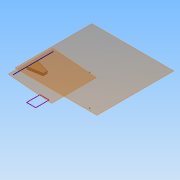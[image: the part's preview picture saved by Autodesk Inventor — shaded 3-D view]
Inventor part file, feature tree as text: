
AUTODESK INVENTOR PART (.ipt)
format: ipt  version: 2015 (Build 190159000, 159)  size: 76,288 bytes
history: native  units: mm
features: sketch x3, other x2, plane x2, extrude x1
ambient origin geometry x8: Origin, YZ Plane, XZ Plane, XY Plane, X Axis, Y Axis, Z Axis, Center Point
bodies: Body1 (feature_tree)
feature tree (8):
  other  "實體1"
  sketch  "草圖1"
  plane  "工作平面1"
  sketch  "草圖2"
  plane  "工作平面2"
  extrude  "擠出1"  [1 undecoded]
  other  "參考1"
  sketch  "草圖3"
note: 1 required parameter value undecoded (feature->parameter linkage not recoverable at this tier; creation-order binding heuristic only, values carry confidence <= 0.55)
